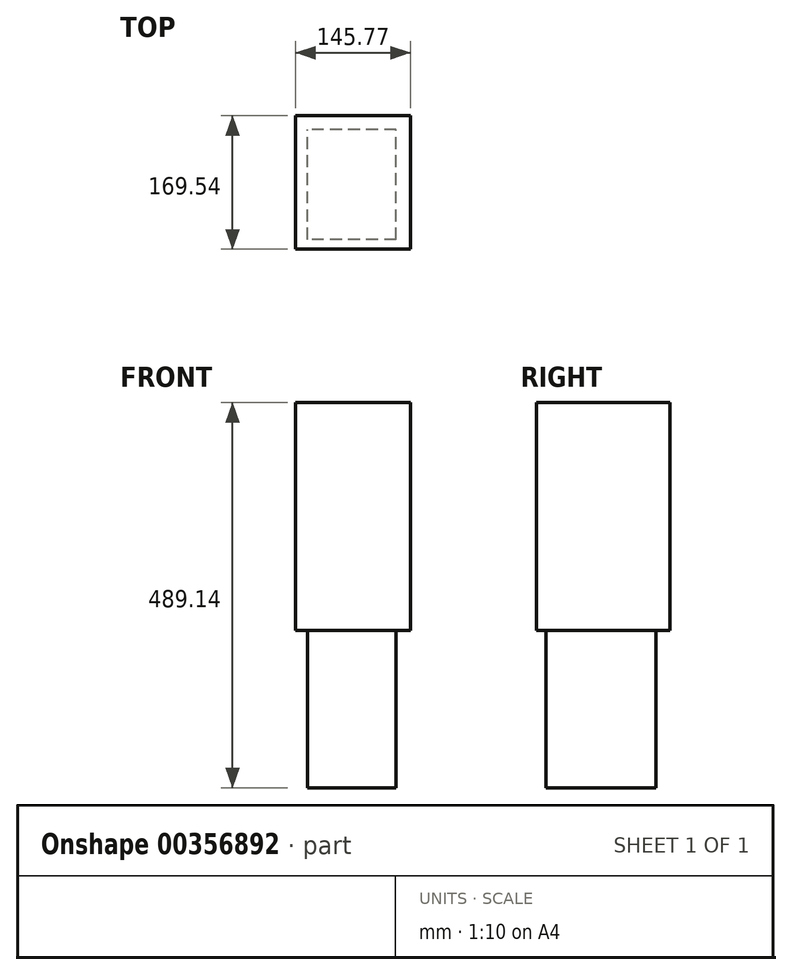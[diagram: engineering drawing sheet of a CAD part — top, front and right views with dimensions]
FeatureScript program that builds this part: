
annotation { "Feature Type Name" : "Feature", "Feature Type Description" : "" }
export const myFeature = defineFeature(function(context is Context, id is Id, definition is map)
    precondition{}
    {
        {
            var Q0;
            Q0=qCreatedBy(makeId("Front.planeOp"),FACE);
            var sketch = newSketch(context, id + "F0", { "sketchPlane" : qUnion([Q0])});
            skLineSegment(sketch, "E0.bottom", {"start": v(-72.63, -72.82) * mm, "end": v(73.14, -72.82) * mm});
            skLineSegment(sketch, "E0.top", {"start": v(-72.63, 0) * mm, "end": v(73.14, 0) * mm});
            skLineSegment(sketch, "E0.left", {"start": v(-72.63, -72.82) * mm, "end": v(-72.63, 0) * mm});
            skLineSegment(sketch, "E0.right", {"start": v(73.14, -72.82) * mm, "end": v(73.14, 0) * mm});
            skSolve(sketch);
        }
        {
            var Q0;
            Q0=makeQuery(id+"F0.imprint","IMPRINT",FACE,{"disambiguationData":[TD([[makeQuery(id+"F0.imprint","IMPRINT",EDGE,{"derivedFrom":sQuery(id+"F0.wireOp",EDGE,"E0.bottom")}),1.0]])]});
            extrude(context, id + "F1", {"entities" : qUnion([Q0]), "oppositeDirection" : true, "depth" : 169.54 * mm});
        }
        {
            var Q0;
            Q0=makeQuery(id+"F1.opExtrude","SWEPT_FACE",FACE,{"disambiguationData":[OSD([sQuery(id+"F0.wireOp",EDGE,"E0.top")])]});
            extrude(context, id + "F2", {"entities" : qUnion([Q0]), "operationType" : NewBodyOperationType.ADD, "depth" : 25.4 * mm});
        }
        {
            var Q0;
            Q0=makeQuery(id+"F2.opExtrude","CAP_FACE",FACE,{"disambiguationData":[OSD([sQuery(id+"F0.wireOp",EDGE,"E0.top")])],"isStart":false});
            extrude(context, id + "F3", {"entities" : qUnion([Q0]), "operationType" : NewBodyOperationType.ADD, "depth" : 191.28 * mm});
        }
        {
            var Q0;
            Q0=makeQuery(id+"F3.opExtrude","CAP_FACE",FACE,{"disambiguationData":[OSD([sQuery(id+"F0.wireOp",EDGE,"E0.top")])],"isStart":false});
            var sketch = newSketch(context, id + "F4", { "sketchPlane" : qUnion([Q0])});
            skLineSegment(sketch, "E1.bottom", {"start": v(-57.24, 152.17) * mm, "end": v(55.06, 152.17) * mm});
            skLineSegment(sketch, "E1.top", {"start": v(-57.24, 12.42) * mm, "end": v(55.06, 12.42) * mm});
            skLineSegment(sketch, "E1.left", {"start": v(-57.24, 152.17) * mm, "end": v(-57.24, 12.42) * mm});
            skLineSegment(sketch, "E1.right", {"start": v(55.06, 152.17) * mm, "end": v(55.06, 12.42) * mm});
            skSolve(sketch);
        }
        {
            var Q0;
            Q0 = qSketchRegion(id + "F4", true);
            extrude(context, id + "F5", {"entities" : qUnion([Q0]), "operationType" : NewBodyOperationType.ADD, "oppositeDirection" : true, "depth" : 489.14 * mm});
        }
    });
